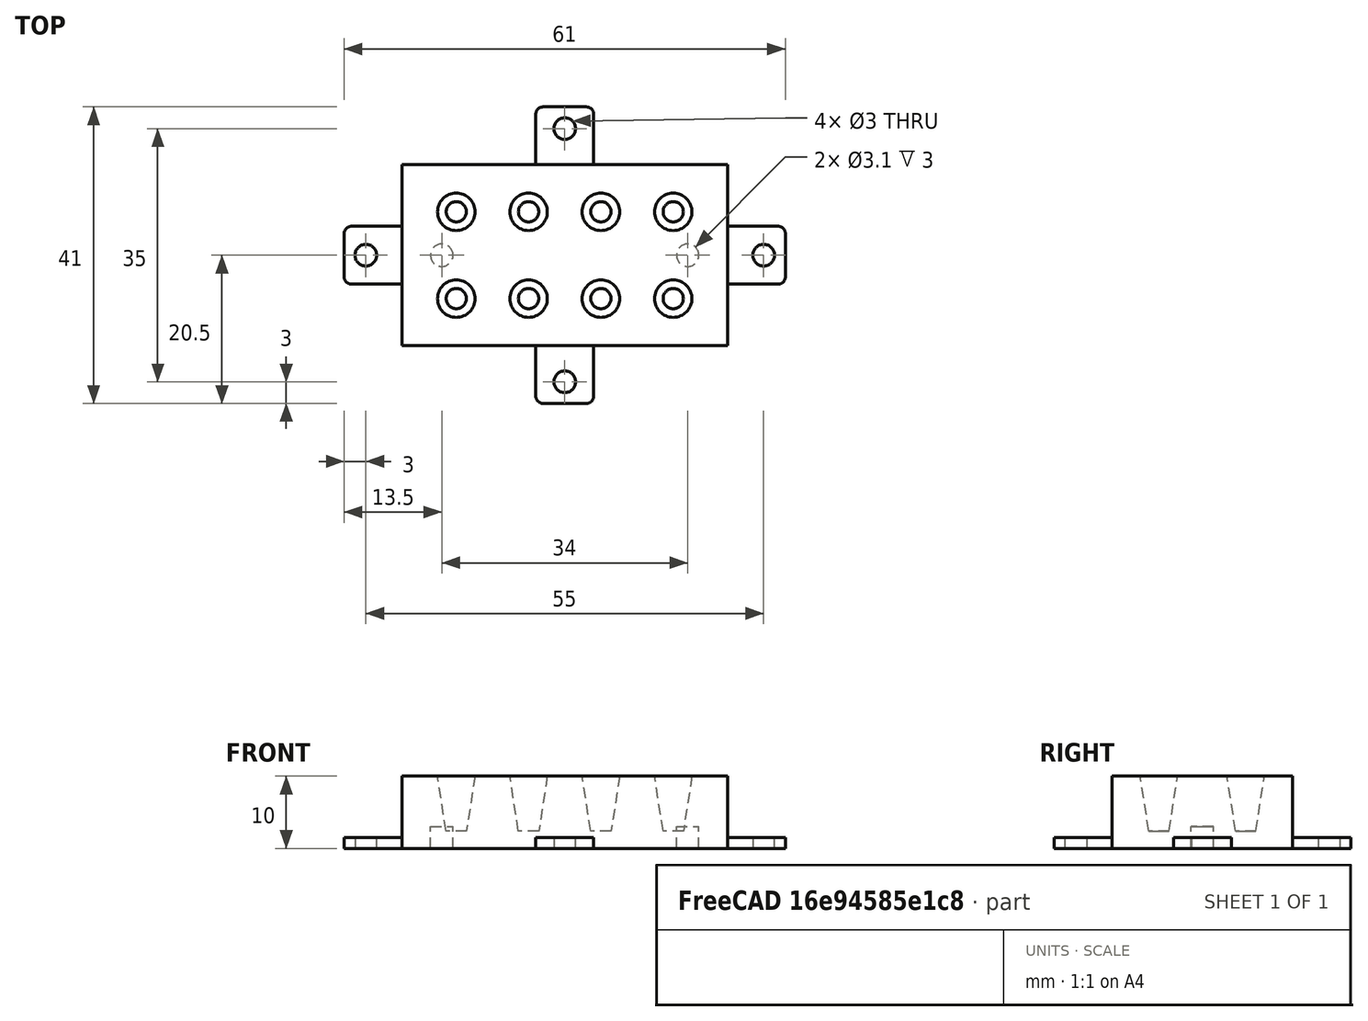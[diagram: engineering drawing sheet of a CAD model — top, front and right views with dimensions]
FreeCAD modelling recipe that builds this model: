
FCSTD DOCUMENT  (FreeCAD 0.18.4R)
Label: JH_tube_holder_v2
License: All rights reserved
LicenseURL: http://en.wikipedia.org/wiki/All_rights_reserved
objects: TechDraw::DrawViewDimension×21, PartDesign::Fillet×8, Sketcher::SketchObject×7, PartDesign::Pad×5, PartDesign::Hole×2, PartDesign::LinearPattern×2, TechDraw::DrawProjGroupItem×2, TechDraw::DrawProjGroup×2, TechDraw::DrawViewSection×2, PartDesign::MultiTransform×1, PartDesign::Body×1, TechDraw::DrawSVGTemplate×1, TechDraw::DrawViewPart×1, TechDraw::DrawViewAnnotation×1, TechDraw::DrawPage×1
note: 33 computed .brp shape members not serialized (recipe doc carries the construction recipe); baked Part::Feature solids carry a one-line shape summary decoded from their .brp

FEATURE [Sketcher::SketchObject] Sketch
  MapMode = 5
  Support = -> [XY_Plane]
  sketch-geometry (4):
    g0: LineSegment StartX=0 StartY=25 StartZ=0 EndX=45 EndY=25 EndZ=0
    g1: LineSegment StartX=45 StartY=25 StartZ=0 EndX=45 EndY=0 EndZ=0
    g2: LineSegment StartX=45 StartY=0 StartZ=0 EndX=0 EndY=0 EndZ=0
    g3: LineSegment StartX=0 StartY=0 StartZ=0 EndX=0 EndY=25 EndZ=0
  constraints (11):
    c: Coincident(g0,g1)
    c: Coincident(g1,g2)
    c: Coincident(g2,g3)
    c: Coincident(g3,g0)
    c: Horizontal(g0)
    c: Horizontal(g2)
    c: Vertical(g1)
    c: Vertical(g3)
    c: DistanceX(g0,g0) = 45  'Largeur'
    c: DistanceY(g1,g1) = 25  'Longueur'
    c: Coincident(g-1,g2)
FEATURE [PartDesign::Pad] Pad
  Length = 10
  Length2 = 100
  Profile = -> Sketch
  Type = 0
FEATURE [Sketcher::SketchObject] Sketch001
  MapMode = 5
  Support = -> [XY_Plane]
  sketch-geometry (2):
    g0: Circle CenterX=5.5 CenterY=12.5 CenterZ=0 NormalX=0 NormalY=0 NormalZ=1 AngleXU=0 Radius=3.2
    g1: Circle CenterX=39.5 CenterY=12.5 CenterZ=0 NormalX=0 NormalY=0 NormalZ=1 AngleXU=0 Radius=3.2
  constraints (6):
    c: DistanceX(g-1,g0) = 5.5
    c: DistanceX(g0,g1) = 34
    c: DistanceY(g-1,g1) = 12.5
    c: DistanceY(g-1,g0) = 12.5
    c: Equal(g1,g0)
    c: Radius(g1) = 3.2
FEATURE [PartDesign::Hole] Hole
  BaseFeature = -> Pad
  Depth = 3
  DepthType = 0
  Diameter = 3.1
  DrillPoint = 0
  DrillPointAngle = 118
  HoleCutCountersinkAngle = 82
  HoleCutDepth = 0
  HoleCutDiameter = 0
  HoleCutType = 0
  ModelActualThread = false
  Profile = -> Sketch001
  Reversed = true
  Tapered = false
  TaperedAngle = 90
  ThreadAngle = 60
  ThreadClass = 1
  ThreadCutOffInner = 0.0649519
  ThreadCutOffOuter = 0.129904
  ThreadDirection = 1
  ThreadFit = 0
  ThreadPitch = 0.6
  ThreadSize = 4
  ThreadType = 4
  Threaded = false
FEATURE [Sketcher::SketchObject] Sketch002
  AttachmentOffset = pos=(0,0,10) rot=(0,0,1;0rad)
  MapMode = 5
  Placement = pos=(0,0,10) rot=(0,0,1;0rad)
  Support = -> [XY_Plane]
  sketch-geometry (1):
    g0: Circle CenterX=7.5 CenterY=6.5 CenterZ=0 NormalX=0 NormalY=0 NormalZ=1 AngleXU=0 Radius=2.59
  constraints (3):
    c: DistanceY(g0) = 6.5
    c: DistanceX(g-1,g0) = 7.5
    c: Radius(g0) = 2.59
FEATURE [PartDesign::Hole] Hole001
  BaseFeature = -> Hole
  Depth = 7.6
  DepthType = 0
  Diameter = 5.18
  DrillPoint = 0
  DrillPointAngle = 118
  HoleCutCountersinkAngle = 90
  HoleCutDepth = 0
  HoleCutDiameter = 0
  HoleCutType = 0
  ModelActualThread = false
  Profile = -> Sketch002
  Tapered = true
  TaperedAngle = 81
  ThreadAngle = 0
  ThreadClass = 0
  ThreadCutOffInner = 0
  ThreadCutOffOuter = 0
  ThreadDirection = 0
  ThreadFit = 0
  ThreadPitch = 0
  ThreadSize = 0
  ThreadType = 0
  Threaded = false
FEATURE [PartDesign::LinearPattern] LinearPattern
  Direction = -> X_Axis
  Length = 30
  Occurrences = 4
FEATURE [PartDesign::LinearPattern] LinearPattern001
  Direction = -> Y_Axis
  Length = 12
  Occurrences = 2
FEATURE [PartDesign::MultiTransform] MultiTransform
  BaseFeature = -> Hole001
  Originals = -> [Hole001]
  Transformations = -> [LinearPattern,LinearPattern001]
FEATURE [Sketcher::SketchObject] CopySketch004
  sketch-geometry (5):
    g0: LineSegment StartX=-8 StartY=16.5 StartZ=0 EndX=0 EndY=16.5 EndZ=0
    g1: LineSegment StartX=0 StartY=16.5 StartZ=0 EndX=0 EndY=8.5 EndZ=0
    g2: LineSegment StartX=0 StartY=8.5 StartZ=0 EndX=-8 EndY=8.5 EndZ=0
    g3: LineSegment StartX=-8 StartY=8.5 StartZ=0 EndX=-8 EndY=16.5 EndZ=0
    g4: Circle CenterX=-5 CenterY=12.5 CenterZ=0 NormalX=0 NormalY=0 NormalZ=1 AngleXU=0 Radius=1.5
  constraints (15):
    c: Coincident(g0,g1)
    c: Coincident(g1,g2)
    c: Coincident(g2,g3)
    c: Coincident(g3,g0)
    c: Horizontal(g0)
    c: Horizontal(g2)
    c: Vertical(g1)
    c: Vertical(g3)
    c: Radius(g4) = 1.5
    c: DistanceY(g1,g1) = 8
    c: DistanceX(g0,g0) = 8
    c: DistanceX(g-1,g1) = 0
    c: DistanceX(g4,g-1) = 5
    c: DistanceY(g-1,g4) = 12.5
    c: DistanceY(g-1,g1) = 8.5
FEATURE [PartDesign::Pad] Pad001
  BaseFeature = -> MultiTransform
  Length = 1.5
  Length2 = 100
  Profile = -> CopySketch004
  Type = 0
FEATURE [Sketcher::SketchObject] CopySketch005
  sketch-geometry (5):
    g0: LineSegment StartX=18.5 StartY=33 StartZ=0 EndX=26.5 EndY=33 EndZ=0
    g1: LineSegment StartX=26.5 StartY=33 StartZ=0 EndX=26.5 EndY=25 EndZ=0
    g2: LineSegment StartX=26.5 StartY=25 StartZ=0 EndX=18.5 EndY=25 EndZ=0
    g3: LineSegment StartX=18.5 StartY=25 StartZ=0 EndX=18.5 EndY=33 EndZ=0
    g4: Circle CenterX=22.5 CenterY=30 CenterZ=0 NormalX=0 NormalY=0 NormalZ=1 AngleXU=0 Radius=1.5
  constraints (14):
    c: Coincident(g0,g1)
    c: Coincident(g1,g2)
    c: Coincident(g2,g3)
    c: Coincident(g3,g0)
    c: Horizontal(g0)
    c: Horizontal(g2)
    c: Vertical(g1)
    c: Vertical(g3)
    c: Radius(g4) = 1.5
    c: DistanceX(g0,g0) = 8
    c: DistanceY(g1,g1) = 8
    c: DistanceY(g-1,g2) = 25
    c: DistanceY(g-1,g4) = 30
    c: DistanceX(g2) = 18.5
FEATURE [PartDesign::Pad] Pad002
  BaseFeature = -> Pad001
  Length = 1.5
  Length2 = 100
  Profile = -> CopySketch005
  Type = 0
FEATURE [Sketcher::SketchObject] CopySketch006
  sketch-geometry (5):
    g0: Circle CenterX=22.5 CenterY=-5 CenterZ=0 NormalX=0 NormalY=0 NormalZ=1 AngleXU=0 Radius=1.5
    g1: LineSegment StartX=18.5 StartY=0 StartZ=0 EndX=26.5 EndY=0 EndZ=0
    g2: LineSegment StartX=26.5 StartY=0 StartZ=0 EndX=26.5 EndY=-8 EndZ=0
    g3: LineSegment StartX=26.5 StartY=-8 StartZ=0 EndX=18.5 EndY=-8 EndZ=0
    g4: LineSegment StartX=18.5 StartY=-8 StartZ=0 EndX=18.5 EndY=0 EndZ=0
  constraints (15):
    c: DistanceX(g0) = 22.5
    c: DistanceY(g0,g-1) = 5
    c: Radius(g0) = 1.5
    c: Coincident(g1,g2)
    c: Coincident(g2,g3)
    c: Coincident(g3,g4)
    c: Coincident(g4,g1)
    c: Horizontal(g1)
    c: Horizontal(g3)
    c: Vertical(g2)
    c: Vertical(g4)
    c: DistanceX(g-1,g1) = 18.5
    c: DistanceY(g1,g-1) = 0
    c: DistanceX(g3,g3) = 8
    c: DistanceY(g2,g1) = 8
FEATURE [PartDesign::Pad] Pad003
  BaseFeature = -> Pad002
  Length = 1.5
  Length2 = 100
  Profile = -> CopySketch006
  Type = 0
FEATURE [Sketcher::SketchObject] CopySketch007
  sketch-geometry (5):
    g0: LineSegment StartX=45 StartY=16.5 StartZ=0 EndX=53 EndY=16.5 EndZ=0
    g1: LineSegment StartX=53 StartY=16.5 StartZ=0 EndX=53 EndY=8.5 EndZ=0
    g2: LineSegment StartX=53 StartY=8.5 StartZ=0 EndX=45 EndY=8.5 EndZ=0
    g3: LineSegment StartX=45 StartY=8.5 StartZ=0 EndX=45 EndY=16.5 EndZ=0
    g4: Circle CenterX=50 CenterY=12.5 CenterZ=0 NormalX=0 NormalY=0 NormalZ=1 AngleXU=0 Radius=1.5
  constraints (15):
    c: Coincident(g0,g1)
    c: Coincident(g1,g2)
    c: Coincident(g2,g3)
    c: Coincident(g3,g0)
    c: Horizontal(g0)
    c: Horizontal(g2)
    c: Vertical(g1)
    c: Vertical(g3)
    c: Radius(g4) = 1.5
    c: DistanceY(g3,g3) = 8
    c: DistanceX(g0,g0) = 8
    c: DistanceY(g-1,g4) = 12.5
    c: DistanceY(g-1,g1) = 8.5
    c: DistanceX(g-1,g0) = 45
    c: DistanceX(g0,g4) = 5
FEATURE [PartDesign::Pad] Pad004
  BaseFeature = -> Pad003
  Length = 1.5
  Length2 = 100
  Profile = -> CopySketch007
  Type = 0
FEATURE [PartDesign::Fillet] Fillet
  Base = -> Pad004 [Edge100]
  BaseFeature = -> Pad004
  Radius = 1
FEATURE [PartDesign::Fillet] Fillet001
  Base = -> Fillet [Edge25]
  BaseFeature = -> Fillet
  Radius = 1
FEATURE [PartDesign::Fillet] Fillet002
  Base = -> Fillet001 [Edge95]
  BaseFeature = -> Fillet001
  Radius = 1
FEATURE [PartDesign::Fillet] Fillet003
  Base = -> Fillet002 [Edge8]
  BaseFeature = -> Fillet002
  Radius = 1
FEATURE [PartDesign::Fillet] Fillet004
  Base = -> Fillet003 [Edge78]
  BaseFeature = -> Fillet003
  Radius = 1
FEATURE [PartDesign::Fillet] Fillet005
  Base = -> Fillet004 [Edge8]
  BaseFeature = -> Fillet004
  Radius = 1
FEATURE [PartDesign::Fillet] Fillet006
  Base = -> Fillet005 [Edge85]
  BaseFeature = -> Fillet005
  Radius = 1
FEATURE [PartDesign::Fillet] Fillet007
  Base = -> Fillet006 [Edge25]
  BaseFeature = -> Fillet006
  Radius = 1
FEATURE [PartDesign::Body] Body
  Group = -> [Sketch,Pad,Sketch001,Hole,Sketch002,Hole001,MultiTransform,LinearPattern,LinearPattern001,Pad001,Pad002,Pad003,Pad004,Fillet,Fillet001,Fillet002,Fillet003,Fillet004,Fillet005,Fillet006,Fillet007]
  Origin = -> Origin
  Tip = -> Fillet007
FEATURE [TechDraw::DrawSVGTemplate] Template
  EditableTexts = Designed_by_Name=Designed by Name; Drawing_number=Drawing number; FC-Date=Date; FC-SC=1.5; FC-SH=Sheet; FC-Title=Title; Subtitle=Subtitle; Weight=Weight
  Height = 210
  Orientation = 1
  Width = 297
FEATURE [TechDraw::DrawProjGroupItem] ProjItem  label="Front"
  CoarseView = false
  Direction = (0,0,1)
  Focus = 100
  HardHidden = false
  IsoCount = 0
  IsoHidden = false
  IsoVisible = false
  LockPosition = true
  Perspective = false
  Rotation = 0
  RotationVector = (1,0,0)
  Scale = 1.5
  ScaleType = 2
  SeamHidden = false
  SeamVisible = false
  SmoothHidden = false
  SmoothVisible = false
  Source = -> [Fillet007]
  Type = 0
  X = 0
  Y = 0
FEATURE [TechDraw::DrawProjGroup] ProjGroup
  Anchor = -> ProjItem
  AutoDistribute = true
  LockPosition = false
  ProjectionType = 2
  Rotation = 0
  Scale = 1.5
  ScaleType = 2
  Source = -> [Fillet007]
  Views = -> [ProjItem]
  X = 88.7887
  Y = 152.632
  spacingX = 15
  spacingY = 15
FEATURE [TechDraw::DrawViewSection] Section  label="Section A - A"
  BaseView = -> ProjItem
  CoarseView = false
  Direction = (0,1,0)
  Focus = 100
  FuseBeforeCut = true
  HardHidden = false
  HatchScale = 1
  IsoCount = 0
  IsoHidden = false
  IsoVisible = false
  LockPosition = false
  NameGeomPattern = Diamond
  Perspective = false
  Rotation = 0
  Scale = 1.5
  ScaleType = 2
  SeamHidden = false
  SeamVisible = false
  SectionDirection = 3
  SectionNormal = (0,1,0)
  SectionOrigin = (22.5,12.5,6)
  SectionSymbol = A
  SmoothHidden = false
  SmoothVisible = false
  Source = -> [Fillet007]
  X = 89.0468
  Y = 98.9802
FEATURE [TechDraw::DrawViewSection] Section001  label="Section B - B"
  BaseView = -> ProjItem
  CoarseView = false
  Direction = (1,0,0)
  Focus = 100
  FuseBeforeCut = true
  HardHidden = false
  HatchScale = 1
  IsoCount = 0
  IsoHidden = false
  IsoVisible = false
  LockPosition = false
  NameGeomPattern = Diamond
  Perspective = false
  Rotation = 90
  Scale = 1.5
  ScaleType = 2
  SeamHidden = false
  SeamVisible = false
  SectionDirection = 1
  SectionNormal = (1,0,0)
  SectionOrigin = (37.5,12.5,5)
  SectionSymbol = B
  SmoothHidden = false
  SmoothVisible = false
  Source = -> [Fillet007]
  X = 181.996
  Y = 153.292
FEATURE [TechDraw::DrawViewDimension] Dimension
  Arbitrary = false
  FormatSpec = %.2f
  LockPosition = false
  MeasureType = 1
  OverTolerance = 0
  References2D = -> [ProjItem]
  Rotation = 0
  ScaleType = 0
  Type = 1
  UnderTolerance = 0
  X = -0.371906
  Y = 43.9777
FEATURE [TechDraw::DrawViewDimension] Dimension001
  Arbitrary = false
  FormatSpec = %.2f
  LockPosition = false
  MeasureType = 1
  OverTolerance = 0
  References2D = -> [ProjItem]
  Rotation = 0
  ScaleType = 0
  Type = 2
  UnderTolerance = 0
  X = -69.4123
  Y = -0.318413
FEATURE [TechDraw::DrawViewDimension] Dimension002
  Arbitrary = false
  FormatSpec = %.2f
  LockPosition = false
  MeasureType = 1
  OverTolerance = 0
  References2D = -> [Section]
  Rotation = 0
  ScaleType = 0
  Type = 2
  UnderTolerance = 0
  X = 14.1504
  Y = -18.1558
FEATURE [TechDraw::DrawViewPart] View001
  CoarseView = false
  Direction = (0,0,-1)
  Focus = 100
  HardHidden = false
  IsoCount = 0
  IsoHidden = false
  IsoVisible = false
  LockPosition = false
  Perspective = false
  Rotation = 0
  Scale = 1.5
  ScaleType = 2
  SeamHidden = false
  SeamVisible = false
  SmoothHidden = false
  SmoothVisible = false
  Source = -> [Body]
  X = 88.8291
  Y = 43.8042
FEATURE [TechDraw::DrawViewAnnotation] Annotation
  Font = osifont
  LineSpace = 80
  LockPosition = false
  MaxWidth = -1
  Rotation = 0
  ScaleType = 0
  Text = Avec filets | UTS #5 
  TextSize = 4
  TextStyle = 0
  X = 34.6537
  Y = 65.823
FEATURE [TechDraw::DrawViewDimension] Dimension004
  Arbitrary = false
  FormatSpec = %.2f
  LockPosition = false
  MeasureType = 1
  OverTolerance = 0
  References2D = -> [View001]
  Rotation = 0
  ScaleType = 0
  Type = 2
  UnderTolerance = 0
  X = -21.3843
  Y = -8.47991
FEATURE [TechDraw::DrawViewDimension] Dimension005
  Arbitrary = false
  FormatSpec = %.2f
  LockPosition = false
  MeasureType = 1
  OverTolerance = 0
  References2D = -> [View001]
  Rotation = 0
  ScaleType = 0
  Type = 1
  UnderTolerance = 0
  X = 1.48396
  Y = 12.1685
FEATURE [TechDraw::DrawViewDimension] Dimension006
  Arbitrary = false
  FormatSpec = %.2f
  LockPosition = false
  MeasureType = 1
  OverTolerance = 0
  References2D = -> [View001]
  Rotation = 0
  ScaleType = 0
  Type = 1
  UnderTolerance = 0
  X = 12.411
  Y = -7.71661
FEATURE [TechDraw::DrawViewDimension] Dimension007
  Arbitrary = false
  FormatSpec = %.2f
  LockPosition = false
  MeasureType = 1
  OverTolerance = 0
  References2D = -> [Section]
  Rotation = 0
  ScaleType = 0
  Type = 2
  UnderTolerance = 0
  X = -66.8833
  Y = 1.6256
FEATURE [TechDraw::DrawViewDimension] Dimension008
  Arbitrary = false
  FormatSpec = %.2f
  LockPosition = false
  MeasureType = 1
  OverTolerance = 0
  References2D = -> [Section]
  Rotation = 0
  ScaleType = 0
  Type = 2
  UnderTolerance = 0
  X = 47.9732
  Y = -15.2331
FEATURE [TechDraw::DrawViewDimension] Dimension009
  Arbitrary = false
  FormatSpec = %.2f
  LockPosition = false
  MeasureType = 1
  OverTolerance = 0
  References2D = -> [Section]
  Rotation = 0
  ScaleType = 0
  Type = 1
  UnderTolerance = 0
  X = 65.1094
  Y = 7.75481
FEATURE [TechDraw::DrawViewDimension] Dimension010
  Arbitrary = false
  FormatSpec = %.2f
  LockPosition = false
  MeasureType = 1
  OverTolerance = 0
  References2D = -> [View001]
  Rotation = 0
  ScaleType = 0
  Type = 2
  UnderTolerance = 0
  X = 47.8115
  Y = -19.9445
FEATURE [TechDraw::DrawViewDimension] Dimension011
  Arbitrary = false
  FormatSpec = %.2f
  LockPosition = false
  MeasureType = 1
  OverTolerance = 0
  References2D = -> [View001]
  Rotation = 0
  ScaleType = 0
  Type = 1
  UnderTolerance = 0
  X = -57.8527
  Y = -25.925
FEATURE [TechDraw::DrawViewDimension] Dimension012
  Arbitrary = false
  FormatSpec = R%.2f
  LockPosition = false
  MeasureType = 1
  OverTolerance = 0
  References2D = -> [View001]
  Rotation = 0
  ScaleType = 0
  Type = 4
  UnderTolerance = 0
  X = -69.5854
  Y = -21.4028
FEATURE [TechDraw::DrawViewDimension] Dimension013
  Arbitrary = false
  FormatSpec = R%.2f
  LockPosition = false
  MeasureType = 1
  OverTolerance = 0
  References2D = -> [View001]
  Rotation = 0
  ScaleType = 0
  Type = 4
  UnderTolerance = 0
  X = -62.4501
  Y = 28.4426
FEATURE [TechDraw::DrawViewDimension] Dimension014
  Arbitrary = false
  FormatSpec = %.2f
  LockPosition = false
  MeasureType = 1
  OverTolerance = 0
  References2D = -> [ProjItem]
  Rotation = 0
  ScaleType = 0
  Type = 1
  UnderTolerance = 0
  X = -52.9827
  Y = 15.7141
FEATURE [TechDraw::DrawViewDimension] Dimension015
  Arbitrary = false
  FormatSpec = %.2f
  LockPosition = false
  MeasureType = 1
  OverTolerance = 0
  References2D = -> [ProjItem]
  Rotation = 0
  ScaleType = 0
  Type = 1
  UnderTolerance = 0
  X = -23.3763
  Y = 31.5562
FEATURE [TechDraw::DrawViewDimension] Dimension016
  Arbitrary = false
  FormatSpec = %.2f
  LockPosition = false
  MeasureType = 1
  OverTolerance = 0
  References2D = -> [ProjItem]
  Rotation = 0
  ScaleType = 0
  Type = 2
  UnderTolerance = 0
  X = 26.0615
  Y = -31.6826
FEATURE [TechDraw::DrawViewDimension] Dimension017
  Arbitrary = false
  FormatSpec = %.2f
  LockPosition = false
  MeasureType = 1
  OverTolerance = 0
  References2D = -> [ProjItem]
  Rotation = 0
  ScaleType = 0
  Type = 1
  UnderTolerance = 0
  X = -32.8076
  Y = -34.5242
FEATURE [TechDraw::DrawViewDimension] Dimension018
  Arbitrary = false
  FormatSpec = %.2f
  LockPosition = false
  MeasureType = 1
  OverTolerance = 0
  References2D = -> [Section001]
  Rotation = 0
  ScaleType = 0
  Type = 1
  UnderTolerance = 0
  X = -19.2467
  Y = -5.27275
FEATURE [TechDraw::DrawViewDimension] Dimension019
  Arbitrary = false
  FormatSpec = %.2f
  LockPosition = false
  MeasureType = 1
  OverTolerance = 0
  References2D = -> [Section001]
  Rotation = 0
  ScaleType = 0
  Type = 1
  UnderTolerance = 0
  X = 32.4155
  Y = 2.12133
FEATURE [TechDraw::DrawViewDimension] Dimension020
  Arbitrary = false
  FormatSpec = %.2f
  LockPosition = false
  MeasureType = 1
  OverTolerance = 0
  References2D = -> [Section001]
  Rotation = 0
  ScaleType = 0
  Type = 2
  UnderTolerance = 0
  X = 11.0221
  Y = 27.1525
FEATURE [TechDraw::DrawViewDimension] Dimension021
  Arbitrary = false
  FormatSpec = %.2f
  LockPosition = false
  MeasureType = 1
  OverTolerance = 0
  References2D = -> [Section001]
  Rotation = 0
  ScaleType = 0
  Type = 2
  UnderTolerance = 0
  X = -18.8013
  Y = 24.9851
FEATURE [TechDraw::DrawProjGroupItem] ProjItem001  label="Front001"
  CoarseView = false
  Direction = (0.324,-0.384,0.865)
  Focus = 100
  HardHidden = false
  IsoCount = 0
  IsoHidden = false
  IsoVisible = false
  LockPosition = true
  Perspective = false
  Rotation = 0
  RotationVector = (0.937,0.254,-0.238)
  Scale = 1.5
  ScaleType = 2
  SeamHidden = false
  SeamVisible = false
  SmoothHidden = false
  SmoothVisible = false
  Source = -> [Fillet006]
  Type = 0
  X = 0
  Y = 0
FEATURE [TechDraw::DrawProjGroup] ProjGroup001
  Anchor = -> ProjItem001
  AutoDistribute = true
  LockPosition = false
  ProjectionType = 0
  Rotation = 0
  Scale = 1.5
  ScaleType = 2
  Source = -> [Fillet006]
  Views = -> [ProjItem001]
  X = 229.494
  Y = 95.1684
  spacingX = 15
  spacingY = 15
FEATURE [TechDraw::DrawPage] Page001
  KeepUpdated = true
  ProjectionType = 0
  Template = -> Template
  Views = -> [ProjGroup,Section,Section001,Dimension,Dimension001,Dimension002,View001,Annotation,Dimension004,Dimension005,Dimension006,Dimension007,Dimension008,Dimension009,Dimension010,Dimension011,Dimension012,Dimension013,Dimension014,Dimension015,Dimension016,Dimension017,Dimension018,Dimension019,Dimension020,Dimension021,ProjGroup001]
